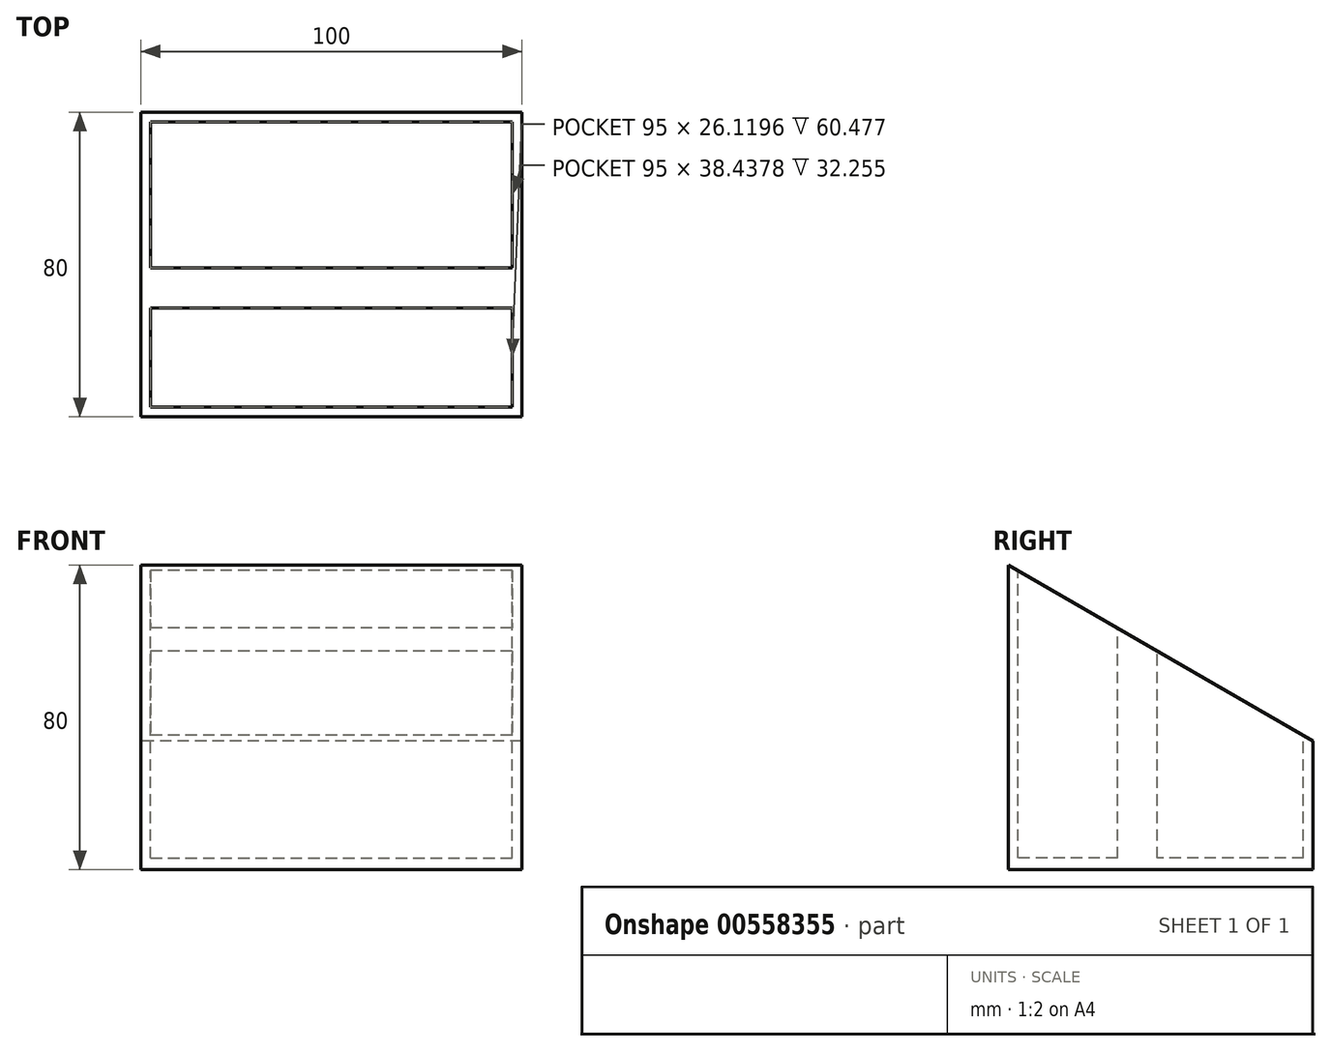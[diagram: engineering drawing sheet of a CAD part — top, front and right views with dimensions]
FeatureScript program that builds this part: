
annotation { "Feature Type Name" : "Feature", "Feature Type Description" : "" }
export const myFeature = defineFeature(function(context is Context, id is Id, definition is map)
    precondition{}
    {
        {
            var Q0;
            Q0=qCreatedBy(makeId("Top.planeOp"),FACE);
            var sketch = newSketch(context, id + "F0", { "sketchPlane" : qUnion([Q0])});
            skLineSegment(sketch, "E0.bottom", {"start": v(-54.28, 32.34) * mm, "end": v(45.72, 32.34) * mm});
            skLineSegment(sketch, "E0.top", {"start": v(-54.28, -17.66) * mm, "end": v(45.72, -17.66) * mm});
            skLineSegment(sketch, "E0.left", {"start": v(-54.28, 32.34) * mm, "end": v(-54.28, -17.66) * mm});
            skLineSegment(sketch, "E0.right", {"start": v(45.72, 32.34) * mm, "end": v(45.72, -17.66) * mm});
            skLineSegment(sketch, "E1.top", {"start": v(-54.28, -47.66) * mm, "end": v(45.72, -47.66) * mm});
            skLineSegment(sketch, "E1.left", {"start": v(-54.28, -17.66) * mm, "end": v(-54.28, -47.66) * mm});
            skLineSegment(sketch, "E1.right", {"start": v(45.72, -17.66) * mm, "end": v(45.72, -47.66) * mm});
            skSolve(sketch);
        }
        {
            var Q0;
            Q0 = qSketchRegion(id + "F0", true);
            extrude(context, id + "F1", {"entities" : qUnion([Q0]), "depth" : 80 * mm, "offsetDistance" : 25 * mm});
        }
        {
            var Q0;
            Q0=makeQuery(id+"F1.opExtrude","CAP_FACE",FACE,{"disambiguationData":[OSD([sQuery(id+"F0.wireOp",EDGE,"E0.bottom"),sQuery(id+"F0.wireOp",EDGE,"E0.left"),sQuery(id+"F0.wireOp",EDGE,"E0.right"),sQuery(id+"F0.wireOp",EDGE,"E0.top"),sQuery(id+"F0.wireOp",EDGE,"E1.top"),sQuery(id+"F0.wireOp",EDGE,"E1.left"),sQuery(id+"F0.wireOp",EDGE,"E1.right")])],"isStart":false});
            var sketch = newSketch(context, id + "F2", { "sketchPlane" : qUnion([Q0])});
            skLineSegment(sketch, "E2.bottom", {"start": v(-51.78, -19.04) * mm, "end": v(43.22, -19.04) * mm});
            skLineSegment(sketch, "E2.top", {"start": v(-51.78, -45.16) * mm, "end": v(43.22, -45.16) * mm});
            skLineSegment(sketch, "E2.left", {"start": v(-51.78, -19.04) * mm, "end": v(-51.78, -45.16) * mm});
            skLineSegment(sketch, "E2.right", {"start": v(43.22, -19.04) * mm, "end": v(43.22, -45.16) * mm});
            skLineSegment(sketch, "E3.bottom", {"start": v(-51.78, 29.84) * mm, "end": v(43.22, 29.84) * mm});
            skLineSegment(sketch, "E3.top", {"start": v(-51.78, -8.6) * mm, "end": v(43.22, -8.6) * mm});
            skLineSegment(sketch, "E3.left", {"start": v(-51.78, 29.84) * mm, "end": v(-51.78, -8.6) * mm});
            skLineSegment(sketch, "E3.right", {"start": v(43.22, 29.84) * mm, "end": v(43.22, -8.6) * mm});
            skSolve(sketch);
        }
        {
            var Q0;
            Q0=makeQuery(id+"F2.imprint","IMPRINT",FACE,{"disambiguationData":[TD([[makeQuery(id+"F2.imprint","IMPRINT",EDGE,{"derivedFrom":sQuery(id+"F2.wireOp",EDGE,"E3.bottom")}),-1.0]])]});
            var Q1;
            Q1=makeQuery(id+"F2.imprint","IMPRINT",FACE,{"disambiguationData":[TD([[makeQuery(id+"F2.imprint","IMPRINT",EDGE,{"derivedFrom":sQuery(id+"F2.wireOp",EDGE,"E2.bottom")}),-1.0]])]});
            extrude(context, id + "F3", {"entities" : qUnion([Q0, Q1]), "operationType" : NewBodyOperationType.REMOVE, "oppositeDirection" : true, "depth" : 77 * mm, "offsetDistance" : 25 * mm});
        }
        {
            var Q0;
            Q0=makeQuery(id+"F1.opExtrude","SWEPT_FACE",FACE,{"disambiguationData":[OSD([sQuery(id+"F0.wireOp",EDGE,"E0.left"),sQuery(id+"F0.wireOp",EDGE,"E1.left")])]});
            var sketch = newSketch(context, id + "F4", { "sketchPlane" : qUnion([Q0])});
            skLineSegment(sketch, "E4", {"start": v(47.66, 80) * mm, "end": v(-32.34, 33.81) * mm});
            skSolve(sketch);
        }
        {
            var Q0;
            {var subQ0=sQuery(id+"F4.wireOp",EDGE,"E4");Q0=makeQuery(id+"F4.imprint","IMPRINT",FACE,{"disambiguationData":[TD([[makeQuery(id+"F4.imprint","IMPRINT",EDGE,{"derivedFrom":subQ0}),-1.0]])]});}
            extrude(context, id + "F5", {"entities" : qUnion([Q0]), "operationType" : NewBodyOperationType.REMOVE, "oppositeDirection" : true, "depth" : 250 * mm, "offsetDistance" : 25 * mm});
        }
    });
